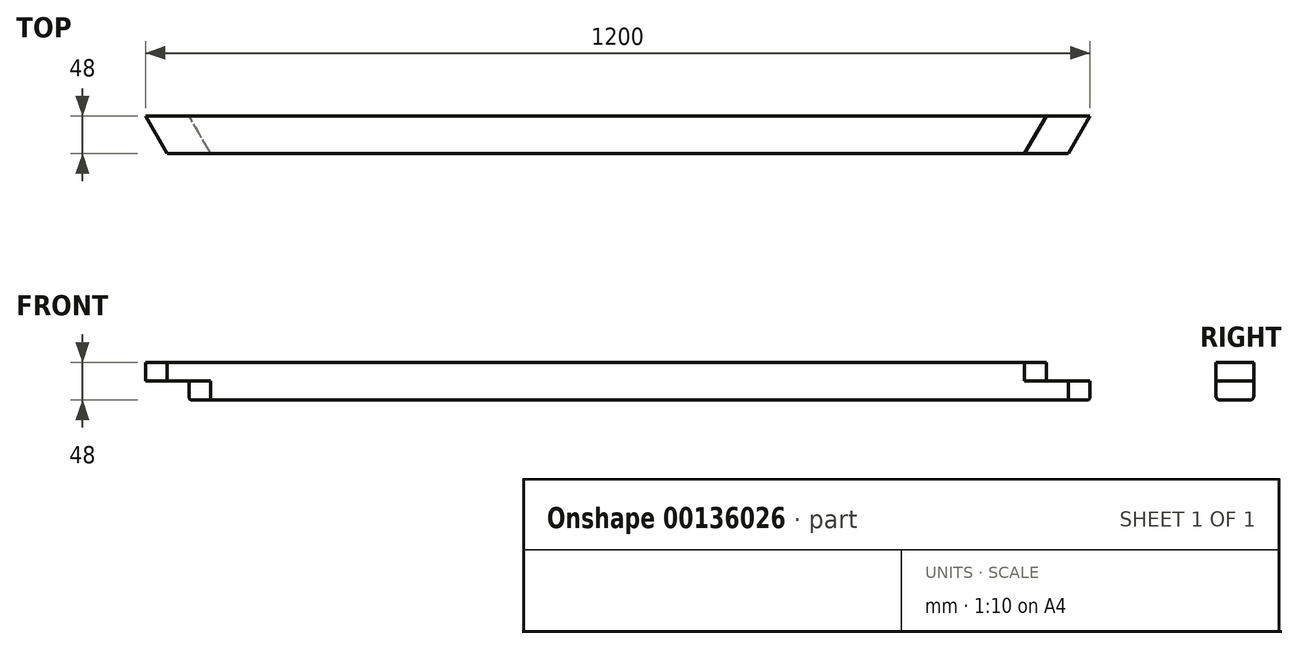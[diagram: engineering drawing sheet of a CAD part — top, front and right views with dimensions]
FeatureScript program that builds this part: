
annotation { "Feature Type Name" : "Feature", "Feature Type Description" : "" }
export const myFeature = defineFeature(function(context is Context, id is Id, definition is map)
    precondition{}
    {
        {
            var Q0;
            Q0=qCreatedBy(makeId("Top.planeOp"),FACE);
            var sketch = newSketch(context, id + "F0", { "sketchPlane" : qUnion([Q0])});
            skLineSegment(sketch, "E0.bottom", {"start": v(600, 24) * mm, "end": v(-600, 24) * mm});
            skLineSegment(sketch, "E0.top", {"start": v(600, -24) * mm, "end": v(-600, -24) * mm});
            skLineSegment(sketch, "E0.left", {"start": v(600, 24) * mm, "end": v(600, -24) * mm});
            skLineSegment(sketch, "E0.right", {"start": v(-600, 24) * mm, "end": v(-600, -24) * mm});
            skPoint(sketch, "E0.middle", {"position": v(0, 0) * mm});
            skLineSegment(sketch, "E1", {"start": v(600, 24) * mm, "end": v(572.29, -24) * mm});
            skLineSegment(sketch, "E2", {"start": v(-600, 24) * mm, "end": v(-572.29, -24) * mm});
            skSolve(sketch);
        }
        {
            var Q0;
            Q0=makeQuery(id+"F0.imprint","IMPRINT",FACE,{"disambiguationData":[TD([[makeQuery(id+"F0.imprint","IMPRINT",EDGE,{"derivedFrom":sQuery(id+"F0.wireOp",EDGE,"E0.bottom")}),1.0]])]});
            extrude(context, id + "F1", {"entities" : qUnion([Q0]), "endBound" : BoundingType.SYMMETRIC, "depth" : 48 * mm});
        }
        {
            var Q0;
            Q0=makeQuery(id+"F1.opExtrude","CAP_FACE",FACE,{"disambiguationData":[OSD([sQuery(id+"F0.wireOp",EDGE,"E0.bottom"),sQuery(id+"F0.wireOp",EDGE,"E0.top"),sQuery(id+"F0.wireOp",EDGE,"E1"),sQuery(id+"F0.wireOp",EDGE,"E2")])],"isStart":false});
            var sketch = newSketch(context, id + "F2", { "sketchPlane" : qUnion([Q0])});
            skLineSegment(sketch, "E3", {"start": v(516.86, -24) * mm, "end": v(544.57, 24) * mm});
            skSolve(sketch);
        }
        {
            var Q0;
            {var subQ0=sQuery(id+"F2.wireOp",EDGE,"E3");Q0=makeQuery(id+"F2.imprint","IMPRINT",FACE,{"disambiguationData":[TD([[makeQuery(id+"F2.imprint","IMPRINT",EDGE,{"derivedFrom":subQ0}),-1.0]])]});}
            extrude(context, id + "F3", {"entities" : qUnion([Q0]), "operationType" : NewBodyOperationType.REMOVE, "oppositeDirection" : true, "depth" : 24 * mm});
        }
        {
            var Q0;
            Q0=makeQuery(id+"F1.opExtrude","CAP_FACE",FACE,{"disambiguationData":[OSD([sQuery(id+"F0.wireOp",EDGE,"E0.bottom"),sQuery(id+"F0.wireOp",EDGE,"E0.top"),sQuery(id+"F0.wireOp",EDGE,"E1"),sQuery(id+"F0.wireOp",EDGE,"E2")])],"isStart":true});
            var sketch = newSketch(context, id + "F4", { "sketchPlane" : qUnion([Q0])});
            skLineSegment(sketch, "E4", {"start": v(-516.86, 24) * mm, "end": v(-544.57, -24) * mm});
            skSolve(sketch);
        }
        {
            var Q0;
            {var subQ0=sQuery(id+"F4.wireOp",EDGE,"E4");Q0=makeQuery(id+"F4.imprint","IMPRINT",FACE,{"disambiguationData":[TD([[makeQuery(id+"F4.imprint","IMPRINT",EDGE,{"derivedFrom":subQ0}),-1.0]])]});}
            extrude(context, id + "F5", {"entities" : qUnion([Q0]), "operationType" : NewBodyOperationType.REMOVE, "oppositeDirection" : true, "depth" : 24 * mm});
        }
        {
            var Q0;
            Q0=makeQuery(id+"F1.opExtrude","CAP_EDGE",EDGE,{"disambiguationData":[OSD([sQuery(id+"F0.wireOp",EDGE,"E0.bottom")])],"isStart":true});
            var Q1;
            Q1=makeQuery(id+"F1.opExtrude","CAP_EDGE",EDGE,{"disambiguationData":[OSD([sQuery(id+"F0.wireOp",EDGE,"E0.top")])],"isStart":true});
            fillet(context, id + "F6", {"entities" : qUnion([Q0, Q1]), "radius" : 5 * mm, "tangentPropagation" : true, "allowEdgeOverflow" : false});
        }
    });
